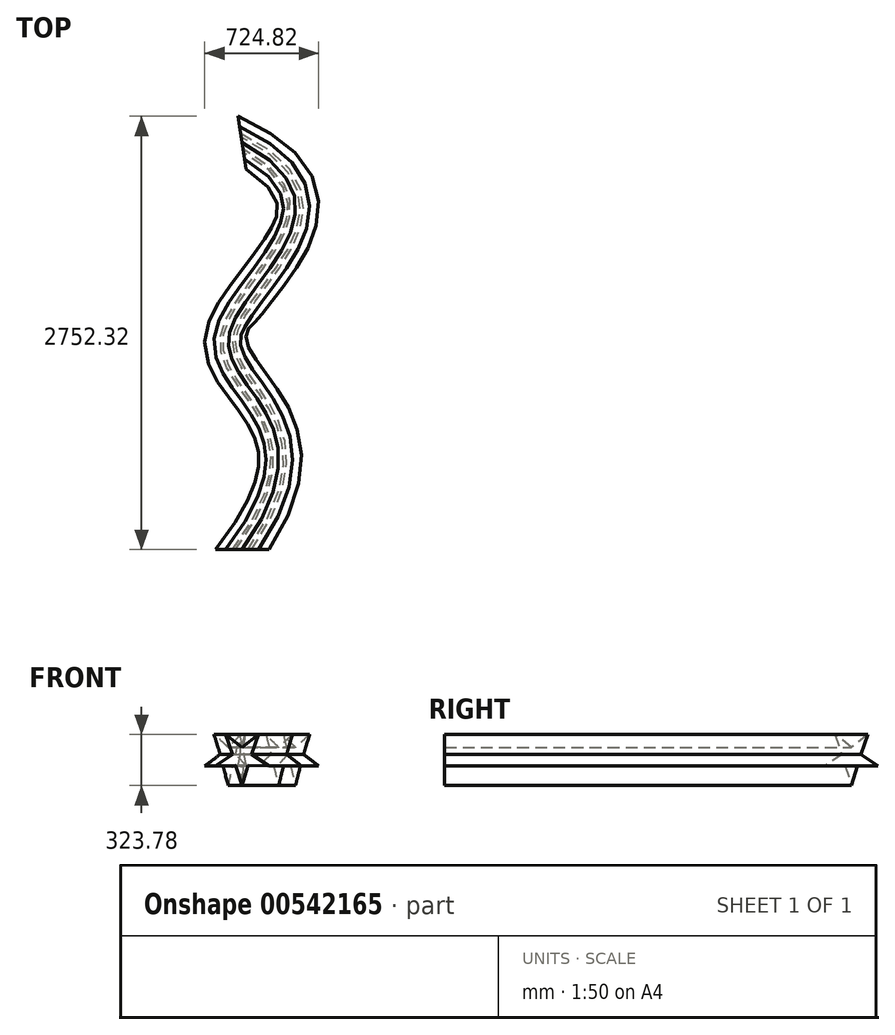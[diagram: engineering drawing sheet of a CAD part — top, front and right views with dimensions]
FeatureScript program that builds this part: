
annotation { "Feature Type Name" : "Feature", "Feature Type Description" : "" }
export const myFeature = defineFeature(function(context is Context, id is Id, definition is map)
    precondition{}
    {
        {
            var Q0;
            Q0=qCreatedBy(makeId("Front.planeOp"),FACE);
            var sketch = newSketch(context, id + "F0", { "sketchPlane" : qUnion([Q0])});
            skPoint(sketch, "E0.0.midPoint", {"position": v(0, 144.8) * mm});
            skLineSegment(sketch, "E1", {"start": v(0, -178.98) * mm, "end": v(37.82, -52.05) * mm});
            skLineSegment(sketch, "E2", {"start": v(37.82, -52.05) * mm, "end": v(170.22, -55.3) * mm});
            skLineSegment(sketch, "E3", {"start": v(170.22, -55.3) * mm, "end": v(61.19, 19.88) * mm});
            skLineSegment(sketch, "E4", {"start": v(61.19, 19.88) * mm, "end": v(105.2, 144.8) * mm});
            skLineSegment(sketch, "E5", {"start": v(105.2, 144.8) * mm, "end": v(0, 64.34) * mm});
            skLineSegment(sketch, "E6", {"start": v(0, 64.34) * mm, "end": v(-105.2, 144.8) * mm});
            skLineSegment(sketch, "E7", {"start": v(-105.2, 144.8) * mm, "end": v(-61.19, 19.88) * mm});
            skLineSegment(sketch, "E8", {"start": v(-61.19, 19.88) * mm, "end": v(-170.22, -55.3) * mm});
            skLineSegment(sketch, "E9", {"start": v(-170.22, -55.3) * mm, "end": v(-40.82, -52.12) * mm});
            skLineSegment(sketch, "E10", {"start": v(-40.82, -52.12) * mm, "end": v(0, -178.98) * mm});
            skSolve(sketch);
        }
        {
            var Q0;
            Q0=qCreatedBy(makeId("Top.planeOp"),FACE);
            var sketch = newSketch(context, id + "F1", { "sketchPlane" : qUnion([Q0])});
            skFitSpline(sketch, "E11", {"points": [v(0, 0) * mm, v(-83.37, 1362.8) * mm, v(0, 2584) * mm], "startDerivative": vector(3482.6, 4781.38) * mm, "endDerivative": vector(-4808.33, 2505.07) * mm});
            skSolve(sketch);
        }
        {
            var Q0;
            Q0=makeQuery(id+"F0.imprint","IMPRINT",FACE,{"disambiguationData":[TD([[makeQuery(id+"F0.imprint","IMPRINT",EDGE,{"derivedFrom":sQuery(id+"F0.wireOp",EDGE,"E1")}),1.0]])]});
            var Q1;
            Q1=sQuery(id+"F1.wireOp",EDGE,"E11");
            sweep(context, id + "F2", {"profiles" : qUnion([Q0]), "path" : qUnion([Q1])});
        }
    });
